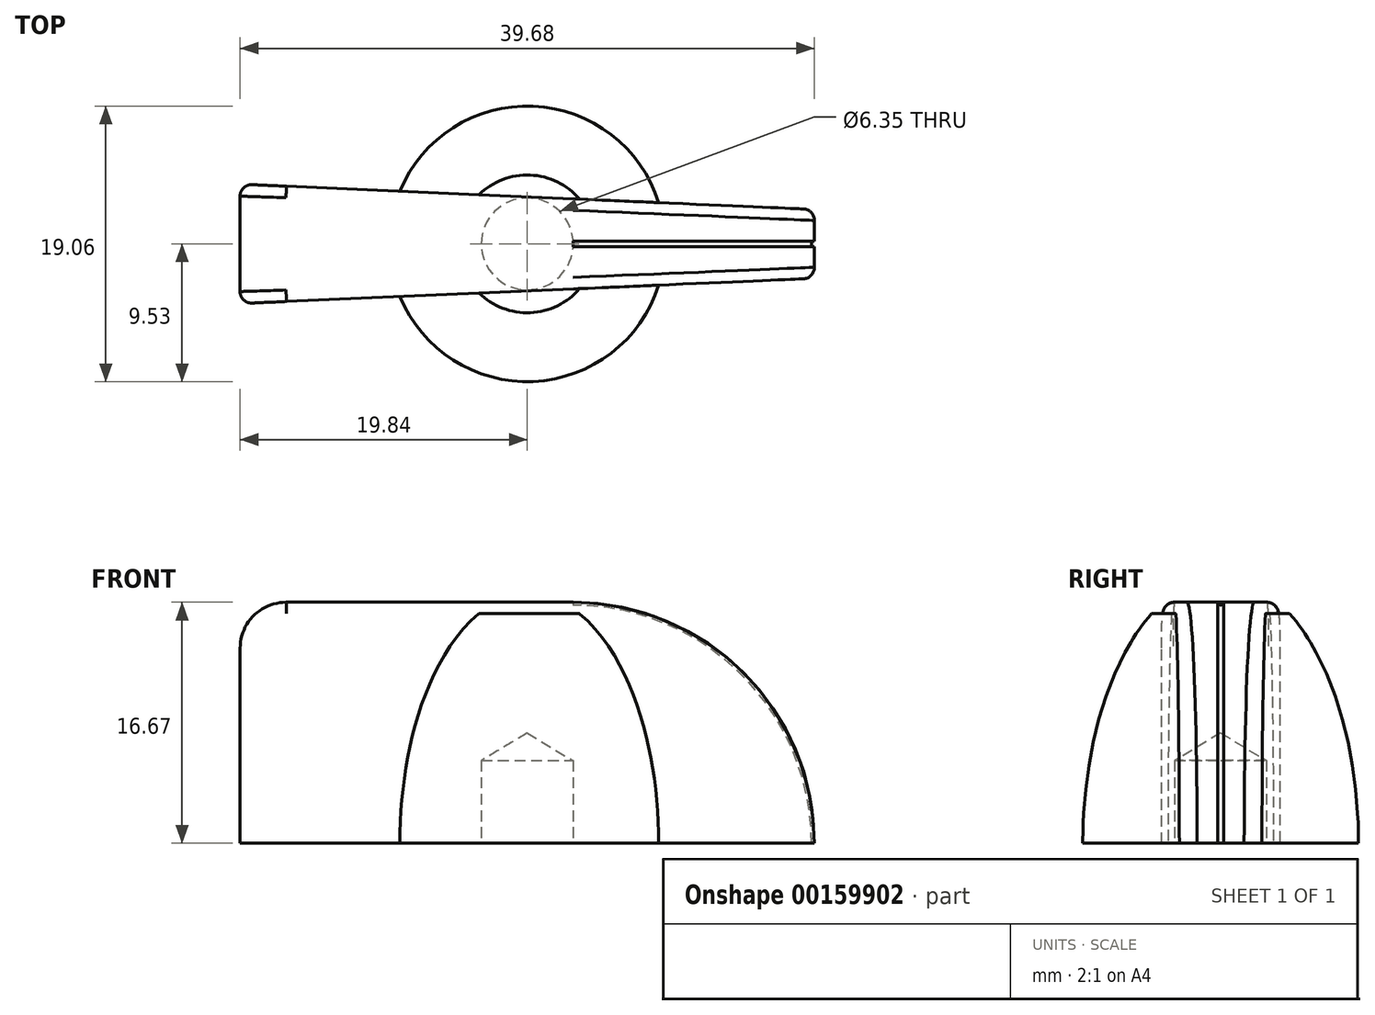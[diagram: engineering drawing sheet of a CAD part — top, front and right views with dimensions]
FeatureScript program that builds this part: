
annotation { "Feature Type Name" : "Feature", "Feature Type Description" : "" }
export const myFeature = defineFeature(function(context is Context, id is Id, definition is map)
    precondition{}
    {
        {
            var Q0;
            Q0=qCreatedBy(makeId("Front.planeOp"),FACE);
            var sketch = newSketch(context, id + "F0", { "sketchPlane" : qUnion([Q0])});
            skLineSegment(sketch, "E0", {"start": v(0, 0) * mm, "end": v(9.53, 0) * mm});
            skLineSegment(sketch, "E1", {"start": v(0, 0) * mm, "end": v(0, 15.88) * mm});
            skLineSegment(sketch, "E2", {"start": v(0, 15.88) * mm, "end": v(4.76, 15.88) * mm});
            skEllipticalArc(sketch, "E3", {});
            const initialGuessF0  = {"E3": [0, 0, 0, 1, 0.018330871046770617, 0.009525, 4.71238898038469, 5.759586531581287]};
            skSetInitialGuess(sketch, initialGuessF0);
            skSolve(sketch);
        }
        {
            var Q0;
            Q0=makeQuery(id+"F0.imprint","IMPRINT",FACE,{"disambiguationData":[TD([[makeQuery(id+"F0.imprint","IMPRINT",EDGE,{"derivedFrom":sQuery(id+"F0.wireOp",EDGE,"E0")}),1.0]])]});
            var Q1;
            Q1=sQuery(id+"F0.wireOp",EDGE,"E1");
            revolve(context, id + "F1", {"entities" : qUnion([Q0]), "axis" : qUnion([Q1]), "revolveType" : RevolveType.FULL});
        }
        {
            var Q0;
            Q0=qCreatedBy(makeId("Top.planeOp"),FACE);
            var sketch = newSketch(context, id + "F2", { "sketchPlane" : qUnion([Q0])});
            skLineSegment(sketch, "E4.right", {"start": v(-19.84, -4.13) * mm, "end": v(-19.84, 4.13) * mm});
            skPoint(sketch, "E4.middle", {"position": v(0, 0) * mm});
            skLineSegment(sketch, "E5", {"start": v(-19.84, 0) * mm, "end": v(0, 0) * mm, "construction": true});
            skLineSegment(sketch, "E6", {"start": v(19.84, 2.38) * mm, "end": v(19.84, -2.38) * mm});
            skLineSegment(sketch, "E7", {"start": v(0, 0) * mm, "end": v(19.84, 0) * mm, "construction": true});
            skLineSegment(sketch, "E8", {"start": v(-19.84, -4.13) * mm, "end": v(19.84, -2.38) * mm});
            skLineSegment(sketch, "E9", {"start": v(-19.84, 4.13) * mm, "end": v(19.84, 2.38) * mm});
            skSolve(sketch);
        }
        {
            var Q0;
            Q0=makeQuery(id+"F2.imprint","IMPRINT",FACE,{"disambiguationData":[TD([[makeQuery(id+"F2.imprint","IMPRINT",EDGE,{"derivedFrom":sQuery(id+"F2.wireOp",EDGE,"E4.right")}),-1.0]])]});
            extrude(context, id + "F3", {"entities" : qUnion([Q0]), "operationType" : NewBodyOperationType.ADD, "depth" : 16.67 * mm});
        }
        {
            var Q0;
            Q0=makeQuery(id+"F3.opExtrude","CAP_EDGE",EDGE,{"disambiguationData":[OSD([sQuery(id+"F2.wireOp",EDGE,"E6")])],"isStart":false});
            fillet(context, id + "F4", {"entities" : qUnion([Q0]), "radius" : 16.67 * mm, "tangentPropagation" : true, "allowEdgeOverflow" : false});
        }
        {
            var Q0;
            Q0=makeQuery(id+"F3.opExtrude","CAP_EDGE",EDGE,{"disambiguationData":[OSD([sQuery(id+"F2.wireOp",EDGE,"E4.right")])],"isStart":false});
            fillet(context, id + "F5", {"entities" : qUnion([Q0]), "radius" : 3.17 * mm, "tangentPropagation" : true, "allowEdgeOverflow" : false});
        }
        {
            var Q0;
            Q0=makeQuery(id+"F3.opExtrude","SWEPT_EDGE",EDGE,{"disambiguationData":[OSD([sQuery(id+"F2.wireOp",EDGE,"E4.right"),sQuery(id+"F2.wireOp",EDGE,"E8")])]});
            var Q1;
            Q1=makeQuery(id+"F4.opFillet","BLEND_EDGE",EDGE,{"blendedFrom":[makeQuery(id+"F3.opExtrude","CAP_EDGE",EDGE,{"disambiguationData":[OSD([sQuery(id+"F2.wireOp",EDGE,"E6")])],"isStart":false}),makeQuery(id+"F3.opExtrude","SWEPT_FACE",FACE,{"disambiguationData":[OSD([sQuery(id+"F2.wireOp",EDGE,"E9")])]})],"blendedInto":[makeQuery(id+"F3.opExtrude","SWEPT_FACE",FACE,{"disambiguationData":[OSD([sQuery(id+"F2.wireOp",EDGE,"E9")])]})]});
            fillet(context, id + "F6", {"entities" : qUnion([Q0, Q1]), "radius" : 0.8 * mm, "tangentPropagation" : true, "allowEdgeOverflow" : false});
        }
        {
            var Q0;
            Q0=qCreatedBy(makeId("Front.planeOp"),FACE);
            var sketch = newSketch(context, id + "F7", { "sketchPlane" : qUnion([Q0])});
            skArc(sketch, "E10.0", {"start": v(3.17, 16.67) * mm, "mid": v(14.96, 11.79) * mm, "end": v(19.84, 0) * mm});
            skSolve(sketch);
        }
        {
            var Q0;
            Q0=makeQuery(id+"F2.imprint","IMPRINT",FACE,{"disambiguationData":[TD([[makeQuery(id+"F2.imprint","IMPRINT",EDGE,{"derivedFrom":sQuery(id+"F2.wireOp",EDGE,"E4.right")}),-1.0]])]});
            var sketch = newSketch(context, id + "F8", { "sketchPlane" : qUnion([Q0])});
            skCircle(sketch, "E11", {"center": v(19.84, 0) * mm, "radius": 0.2 * mm});
            skSolve(sketch);
        }
        {
            var Q0;
            {var subQ0=sQuery(id+"F8.wireOp",EDGE,"E11");var subQ1=makeQuery(id+"F2.imprint","IMPRINT",EDGE,{"derivedFrom":sQuery(id+"F2.wireOp",EDGE,"E6")});var subQ2=makeQuery(id+"F8.imprint","INTERSECT",VERTEX,{"disambiguationData":[OD(0.0)],"derivedFrom":[subQ1,subQ0]});Q0=makeQuery(id+"F8.imprint","IMPRINT",FACE,{"disambiguationData":[TD([[makeQuery(id+"F8.imprint","IMPRINT",EDGE,{"disambiguationData":[TD([[subQ2,-1.0]])],"derivedFrom":subQ0}),1.0]])]});}
            var Q1;
            Q1=sQuery(id+"F7.wireOp",EDGE,"E10.0");
            sweep(context, id + "F9", {"operationType" : NewBodyOperationType.REMOVE, "profiles" : qUnion([Q0]), "path" : qUnion([Q1])});
        }
        {
            var Q0;
            Q0=makeQuery(id+"F3.boolean.opBoolean","MERGE",FACE,{"derivedFrom":[makeQuery(id+"F1.opRevolve","SWEPT_FACE",FACE,{"disambiguationData":[OSD([sQuery(id+"F0.wireOp",EDGE,"E0")])]}),makeQuery(id+"F3.opExtrude","CAP_FACE",FACE,{"disambiguationData":[OSD([sQuery(id+"F2.wireOp",EDGE,"E4.right"),sQuery(id+"F2.wireOp",EDGE,"E6"),sQuery(id+"F2.wireOp",EDGE,"E8"),sQuery(id+"F2.wireOp",EDGE,"E9")])],"isStart":true})]});
            var sketch = newSketch(context, id + "F10", { "sketchPlane" : qUnion([Q0])});
            skPoint(sketch, "E12", {"position": v(0, 0) * mm});
            skSolve(sketch);
        }
        {
            var Q0;
            Q0=sQuery(id+"F10.wireOp",VERTEX,"E12");
            var Q1;
            Q1=makeQuery(id+"F1.opRevolve","SWEPT_BODY",BODY,{"disambiguationData":[OSD([sQuery(id+"F0.wireOp",EDGE,"E0"),sQuery(id+"F0.wireOp",EDGE,"E1"),sQuery(id+"F0.wireOp",EDGE,"E2"),sQuery(id+"F0.wireOp",EDGE,"E3")])]});
            hole(context, id + "F11", {"style" : HoleStyle.SIMPLE, "endStyle" : HoleEndStyle.BLIND, "holeDiameter" : 6.35 * mm, "holeDepth" : 5.7 * mm, "locations" : qUnion([Q0]), "scope" : qUnion([Q1])});
        }
    });
